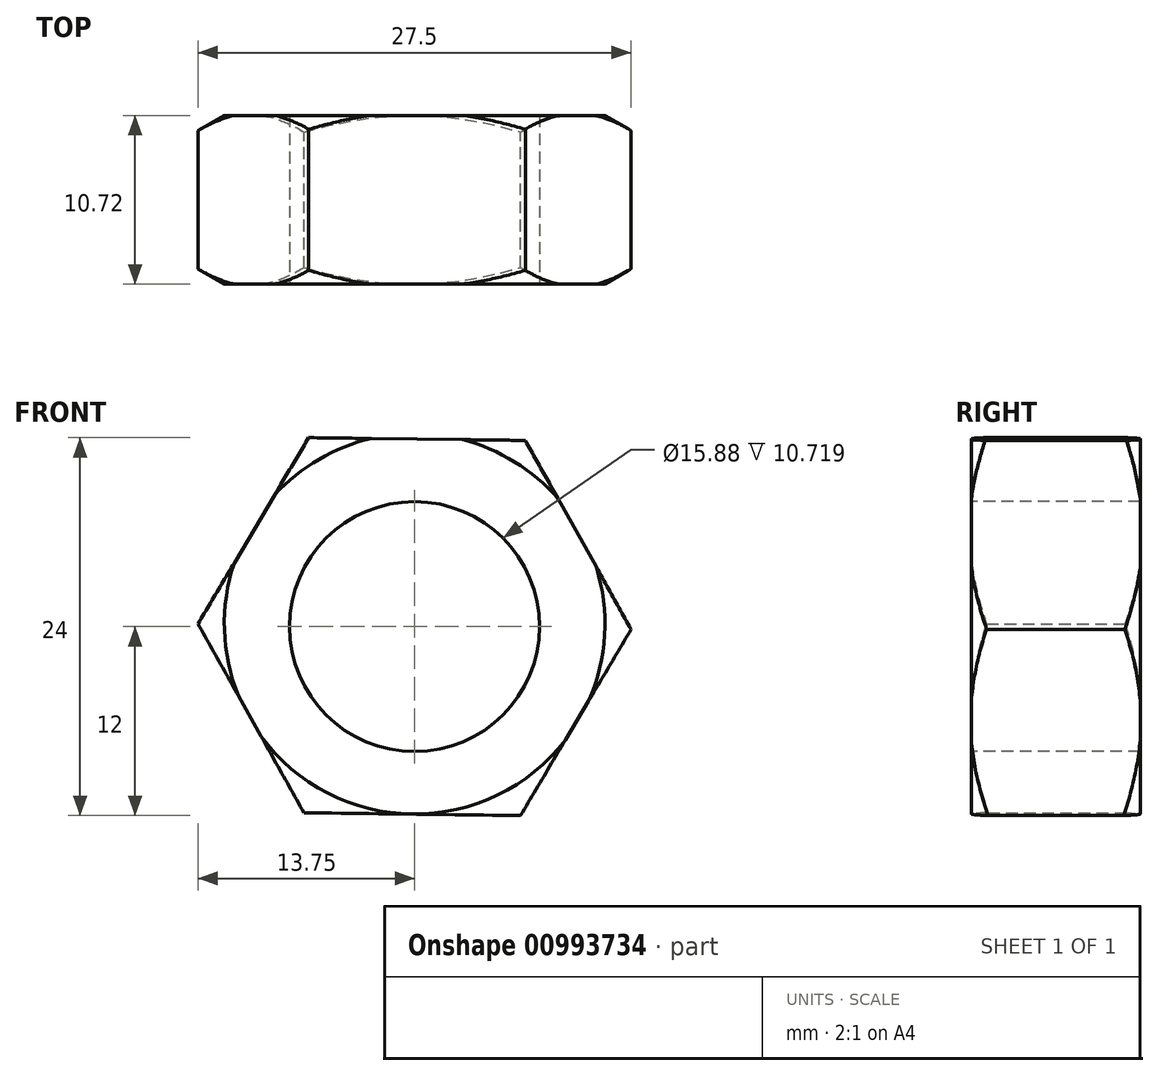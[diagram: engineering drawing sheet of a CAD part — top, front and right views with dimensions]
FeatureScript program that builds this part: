
annotation { "Feature Type Name" : "Feature", "Feature Type Description" : "" }
export const myFeature = defineFeature(function(context is Context, id is Id, definition is map)
    precondition{}
    {
        {
            var Q0;
            Q0=qCreatedBy(makeId("Front.planeOp"),FACE);
            var sketch = newSketch(context, id + "F0", { "sketchPlane" : qUnion([Q0])});
            skCircle(sketch, "E0.cCircle", {"center": v(0, 0) * mm, "radius": 11.91 * mm, "construction": true});
            skLineSegment(sketch, "E0.0", {"start": v(-7.03, -11.82) * mm, "end": v(-13.75, 0.18) * mm});
            skLineSegment(sketch, "E0.1", {"start": v(-13.75, 0.18) * mm, "end": v(-6.72, 12) * mm});
            skLineSegment(sketch, "E0.2", {"start": v(-6.72, 12) * mm, "end": v(7.03, 11.82) * mm});
            skLineSegment(sketch, "E0.3", {"start": v(7.03, 11.82) * mm, "end": v(13.75, -0.18) * mm});
            skLineSegment(sketch, "E0.4", {"start": v(13.75, -0.18) * mm, "end": v(6.72, -12) * mm});
            skLineSegment(sketch, "E0.5", {"start": v(6.72, -12) * mm, "end": v(-7.03, -11.82) * mm});
            skPoint(sketch, "E0.0.midPoint", {"position": v(-10.4, -5.82) * mm});
            skSolve(sketch);
        }
        {
            var Q0;
            Q0 = qSketchRegion(id + "F0", true);
            extrude(context, id + "F1", {"entities" : qUnion([Q0]), "depth" : 10.72 * mm, "offsetDistance" : 25.4 * mm});
        }
        {
            var Q0;
            Q0=makeQuery(id+"F1.opExtrude","CAP_FACE",FACE,{"disambiguationData":[OSD([sQuery(id+"F0.wireOp",EDGE,"E0.0"),sQuery(id+"F0.wireOp",EDGE,"E0.1"),sQuery(id+"F0.wireOp",EDGE,"E0.2"),sQuery(id+"F0.wireOp",EDGE,"E0.3"),sQuery(id+"F0.wireOp",EDGE,"E0.4"),sQuery(id+"F0.wireOp",EDGE,"E0.5")])],"isStart":false});
            var sketch = newSketch(context, id + "F2", { "sketchPlane" : qUnion([Q0])});
            skCircle(sketch, "E1", {"center": v(0, 0) * mm, "radius": 7.94 * mm});
            skSolve(sketch);
        }
        {
            var Q0;
            Q0=makeQuery(id+"F2.imprint","IMPRINT",FACE,{"disambiguationData":[TD([[makeQuery(id+"F2.imprint","IMPRINT",EDGE,{"derivedFrom":sQuery(id+"F2.wireOp",EDGE,"E1")}),1.0]])]});
            extrude(context, id + "F3", {"entities" : qUnion([Q0]), "operationType" : NewBodyOperationType.REMOVE, "endBound" : BoundingType.THROUGH_ALL, "oppositeDirection" : true, "depth" : 25.4 * mm, "offsetDistance" : 25.4 * mm});
        }
        {
            var Q0;
            Q0=qCreatedBy(makeId("Right.planeOp"),FACE);
            var sketch = newSketch(context, id + "F4", { "sketchPlane" : qUnion([Q0])});
            skLineSegment(sketch, "E2", {"start": v(0, 0.18) * mm, "end": v(-10.72, 0.18) * mm, "construction": true});
            skLineSegment(sketch, "E3", {"start": v(-5.36, 0.18) * mm, "end": v(-5.36, -11.82) * mm, "construction": true});
            skLineSegment(sketch, "E4", {"start": v(-10.72, -11.91) * mm, "end": v(-10.72, -19.12) * mm});
            skLineSegment(sketch, "E5", {"start": v(-10.72, -19.12) * mm, "end": v(-6.55, -19.12) * mm});
            skLineSegment(sketch, "E6", {"start": v(-6.55, -19.12) * mm, "end": v(-10.72, -11.91) * mm});
            skLineSegment(sketch, "E7.MirrorCS", {"start": v(-4.16, -19.12) * mm, "end": v(0, -11.91) * mm});
            skLineSegment(sketch, "E8.MirrorCS", {"start": v(0, -11.91) * mm, "end": v(0, -19.12) * mm});
            skLineSegment(sketch, "E9.MirrorCS", {"start": v(0, -19.12) * mm, "end": v(-4.16, -19.12) * mm});
            skSolve(sketch);
        }
        {
            var Q0;
            Q0=makeQuery(id+"F4.imprint","IMPRINT",FACE,{"disambiguationData":[TD([[makeQuery(id+"F4.imprint","IMPRINT",EDGE,{"derivedFrom":sQuery(id+"F4.wireOp",EDGE,"E4")}),1.0]])]});
            var Q1;
            Q1=makeQuery(id+"F4.imprint","IMPRINT",FACE,{"disambiguationData":[TD([[makeQuery(id+"F4.imprint","IMPRINT",EDGE,{"derivedFrom":sQuery(id+"F4.wireOp",EDGE,"E7.MirrorCS")}),-1.0]])]});
            var Q2;
            Q2=sQuery(id+"F4.wireOp",EDGE,"E2");
            revolve(context, id + "F5", {"operationType" : NewBodyOperationType.REMOVE, "surfaceOperationType" : NewSurfaceOperationType.NEW, "entities" : qUnion([Q0, Q1]), "axis" : qUnion([Q2]), "revolveType" : RevolveType.FULL, "oppositeDirection" : true});
        }
    });
